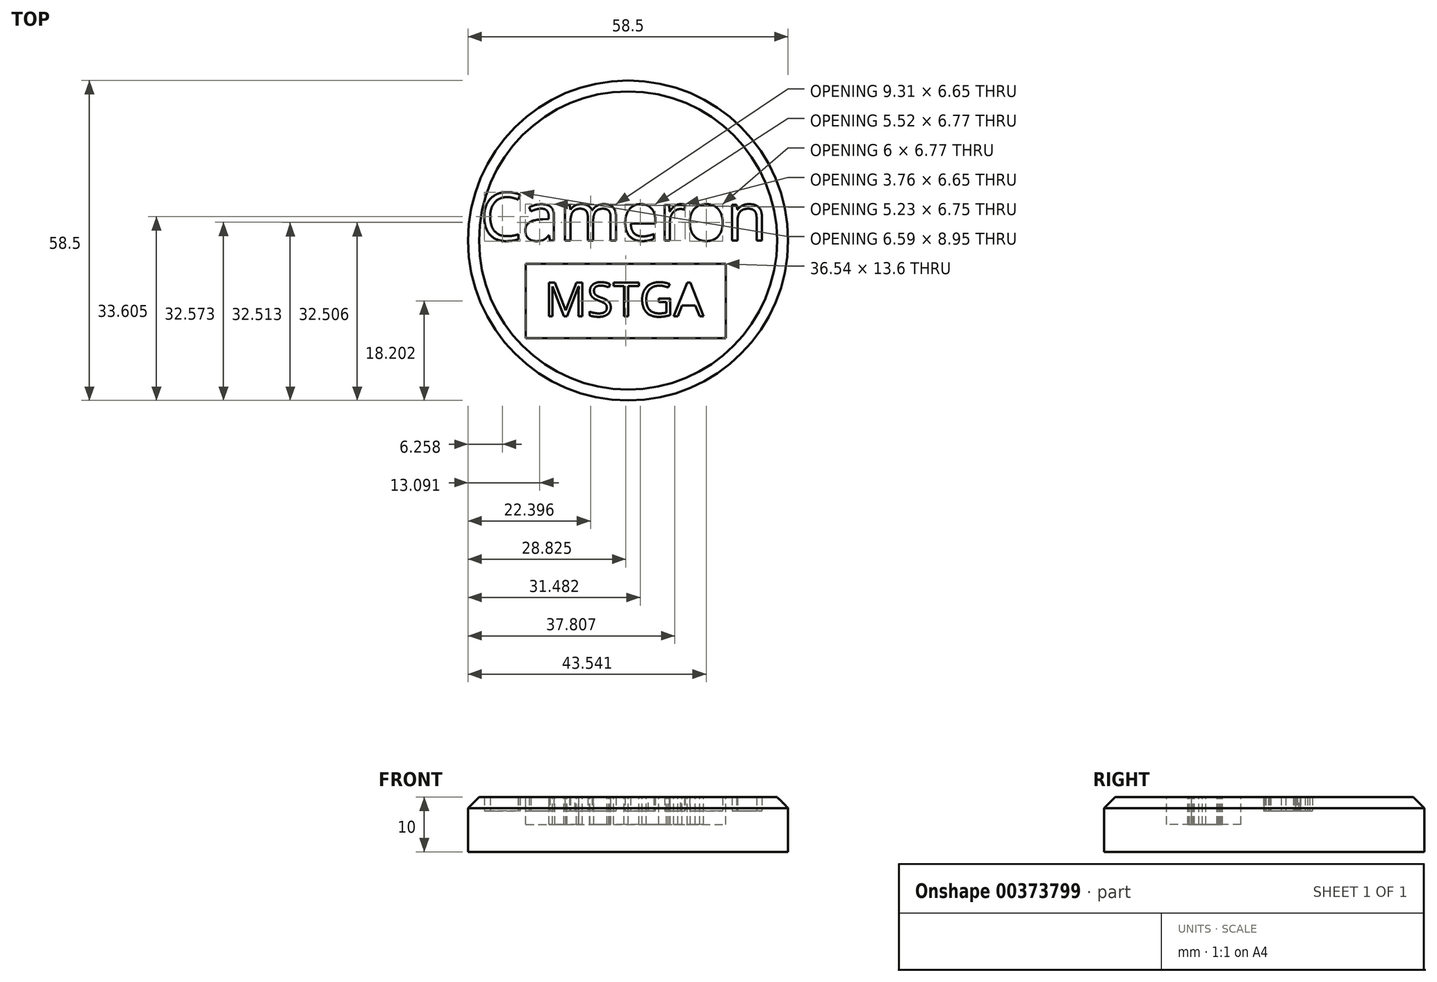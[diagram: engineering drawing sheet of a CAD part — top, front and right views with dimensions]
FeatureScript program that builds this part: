
annotation { "Feature Type Name" : "Feature", "Feature Type Description" : "" }
export const myFeature = defineFeature(function(context is Context, id is Id, definition is map)
    precondition{}
    {
        {
            var Q0;
            Q0=qCreatedBy(makeId("Top.planeOp"),FACE);
            var sketch = newSketch(context, id + "F0", { "sketchPlane" : qUnion([Q0])});
            skCircle(sketch, "E0", {"center": v(0, 0) * mm, "radius": 29.25 * mm});
            skSolve(sketch);
        }
        {
            var Q0;
            Q0=makeQuery(id+"F0.imprint","IMPRINT",FACE,{"disambiguationData":[TD([[makeQuery(id+"F0.imprint","IMPRINT",EDGE,{"derivedFrom":sQuery(id+"F0.wireOp",EDGE,"E0")}),1.0]])]});
            extrude(context, id + "F1", {"entities" : qUnion([Q0]), "depth" : 7.5 * mm});
        }
        {
            var Q0;
            Q0=makeQuery(id+"F1.opExtrude","CAP_FACE",FACE,{"disambiguationData":[OSD([sQuery(id+"F0.wireOp",EDGE,"E0")])],"isStart":false});
            var sketch = newSketch(context, id + "F2", { "sketchPlane" : qUnion([Q0])});
            skText(sketch, "E1", { "text": "Cameron", "fontName": "OpenSans-Regular.ttf"});
            const initialGuessF2  = {"E1": [-0.02703, 0, 1, 0, 0.00878]};
            skSetInitialGuess(sketch, initialGuessF2);
            skSolve(sketch);
        }
        {
            var Q0;
            Q0=makeQuery(id+"F2.imprint","IMPRINT",FACE,{"disambiguationData":[TD([[makeQuery(id+"F2.imprint","IMPRINT",EDGE,{"derivedFrom":sQuery(id+"F2.wireOp",EDGE,"E1.sketch_text.stroke-0")}),1.0]])]});
            extrude(context, id + "F3", {"entities" : qUnion([Q0]), "operationType" : NewBodyOperationType.ADD, "depth" : 2.5 * mm});
        }
        {
            var Q0;
            Q0=makeQuery(id+"F3.opExtrude","CAP_FACE",FACE,{"disambiguationData":[OSD([sQuery(id+"F0.wireOp",EDGE,"E0"),sQuery(id+"F2.wireOp",EDGE,"E1.sketch_text.stroke-0"),sQuery(id+"F2.wireOp",EDGE,"E1.sketch_text.stroke-1"),sQuery(id+"F2.wireOp",EDGE,"E1.sketch_text.stroke-2"),sQuery(id+"F2.wireOp",EDGE,"E1.sketch_text.stroke-3"),sQuery(id+"F2.wireOp",EDGE,"E1.sketch_text.stroke-4"),sQuery(id+"F2.wireOp",EDGE,"E1.sketch_text.stroke-5"),sQuery(id+"F2.wireOp",EDGE,"E1.sketch_text.stroke-6"),sQuery(id+"F2.wireOp",EDGE,"E1.sketch_text.stroke-7"),sQuery(id+"F2.wireOp",EDGE,"E1.sketch_text.stroke-8"),sQuery(id+"F2.wireOp",EDGE,"E1.sketch_text.stroke-9"),sQuery(id+"F2.wireOp",EDGE,"E1.sketch_text.stroke-10"),sQuery(id+"F2.wireOp",EDGE,"E1.sketch_text.stroke-11"),sQuery(id+"F2.wireOp",EDGE,"E1.sketch_text.stroke-12"),sQuery(id+"F2.wireOp",EDGE,"E1.sketch_text.stroke-13"),sQuery(id+"F2.wireOp",EDGE,"E1.sketch_text.stroke-14"),sQuery(id+"F2.wireOp",EDGE,"E1.sketch_text.stroke-15"),sQuery(id+"F2.wireOp",EDGE,"E1.sketch_text.stroke-16"),sQuery(id+"F2.wireOp",EDGE,"E1.sketch_text.stroke-17"),sQuery(id+"F2.wireOp",EDGE,"E1.sketch_text.stroke-18"),sQuery(id+"F2.wireOp",EDGE,"E1.sketch_text.stroke-19"),sQuery(id+"F2.wireOp",EDGE,"E1.sketch_text.stroke-20"),sQuery(id+"F2.wireOp",EDGE,"E1.sketch_text.stroke-21"),sQuery(id+"F2.wireOp",EDGE,"E1.sketch_text.stroke-22"),sQuery(id+"F2.wireOp",EDGE,"E1.sketch_text.stroke-23"),sQuery(id+"F2.wireOp",EDGE,"E1.sketch_text.stroke-24"),sQuery(id+"F2.wireOp",EDGE,"E1.sketch_text.stroke-25"),sQuery(id+"F2.wireOp",EDGE,"E1.sketch_text.stroke-26"),sQuery(id+"F2.wireOp",EDGE,"E1.sketch_text.stroke-27"),sQuery(id+"F2.wireOp",EDGE,"E1.sketch_text.stroke-28"),sQuery(id+"F2.wireOp",EDGE,"E1.sketch_text.stroke-29"),sQuery(id+"F2.wireOp",EDGE,"E1.sketch_text.stroke-30"),sQuery(id+"F2.wireOp",EDGE,"E1.sketch_text.stroke-31"),sQuery(id+"F2.wireOp",EDGE,"E1.sketch_text.stroke-32"),sQuery(id+"F2.wireOp",EDGE,"E1.sketch_text.stroke-33"),sQuery(id+"F2.wireOp",EDGE,"E1.sketch_text.stroke-42"),sQuery(id+"F2.wireOp",EDGE,"E1.sketch_text.stroke-43"),sQuery(id+"F2.wireOp",EDGE,"E1.sketch_text.stroke-44"),sQuery(id+"F2.wireOp",EDGE,"E1.sketch_text.stroke-45"),sQuery(id+"F2.wireOp",EDGE,"E1.sketch_text.stroke-46"),sQuery(id+"F2.wireOp",EDGE,"E1.sketch_text.stroke-47"),sQuery(id+"F2.wireOp",EDGE,"E1.sketch_text.stroke-48"),sQuery(id+"F2.wireOp",EDGE,"E1.sketch_text.stroke-49"),sQuery(id+"F2.wireOp",EDGE,"E1.sketch_text.stroke-50"),sQuery(id+"F2.wireOp",EDGE,"E1.sketch_text.stroke-51"),sQuery(id+"F2.wireOp",EDGE,"E1.sketch_text.stroke-52"),sQuery(id+"F2.wireOp",EDGE,"E1.sketch_text.stroke-53"),sQuery(id+"F2.wireOp",EDGE,"E1.sketch_text.stroke-54"),sQuery(id+"F2.wireOp",EDGE,"E1.sketch_text.stroke-55"),sQuery(id+"F2.wireOp",EDGE,"E1.sketch_text.stroke-56"),sQuery(id+"F2.wireOp",EDGE,"E1.sketch_text.stroke-57"),sQuery(id+"F2.wireOp",EDGE,"E1.sketch_text.stroke-58"),sQuery(id+"F2.wireOp",EDGE,"E1.sketch_text.stroke-59"),sQuery(id+"F2.wireOp",EDGE,"E1.sketch_text.stroke-60"),sQuery(id+"F2.wireOp",EDGE,"E1.sketch_text.stroke-61"),sQuery(id+"F2.wireOp",EDGE,"E1.sketch_text.stroke-62"),sQuery(id+"F2.wireOp",EDGE,"E1.sketch_text.stroke-63"),sQuery(id+"F2.wireOp",EDGE,"E1.sketch_text.stroke-64"),sQuery(id+"F2.wireOp",EDGE,"E1.sketch_text.stroke-65"),sQuery(id+"F2.wireOp",EDGE,"E1.sketch_text.stroke-66"),sQuery(id+"F2.wireOp",EDGE,"E1.sketch_text.stroke-67"),sQuery(id+"F2.wireOp",EDGE,"E1.sketch_text.stroke-68"),sQuery(id+"F2.wireOp",EDGE,"E1.sketch_text.stroke-69"),sQuery(id+"F2.wireOp",EDGE,"E1.sketch_text.stroke-70"),sQuery(id+"F2.wireOp",EDGE,"E1.sketch_text.stroke-71"),sQuery(id+"F2.wireOp",EDGE,"E1.sketch_text.stroke-72"),sQuery(id+"F2.wireOp",EDGE,"E1.sketch_text.stroke-73"),sQuery(id+"F2.wireOp",EDGE,"E1.sketch_text.stroke-74"),sQuery(id+"F2.wireOp",EDGE,"E1.sketch_text.stroke-75"),sQuery(id+"F2.wireOp",EDGE,"E1.sketch_text.stroke-76"),sQuery(id+"F2.wireOp",EDGE,"E1.sketch_text.stroke-77"),sQuery(id+"F2.wireOp",EDGE,"E1.sketch_text.stroke-78"),sQuery(id+"F2.wireOp",EDGE,"E1.sketch_text.stroke-79"),sQuery(id+"F2.wireOp",EDGE,"E1.sketch_text.stroke-80"),sQuery(id+"F2.wireOp",EDGE,"E1.sketch_text.stroke-81"),sQuery(id+"F2.wireOp",EDGE,"E1.sketch_text.stroke-82"),sQuery(id+"F2.wireOp",EDGE,"E1.sketch_text.stroke-83"),sQuery(id+"F2.wireOp",EDGE,"E1.sketch_text.stroke-89"),sQuery(id+"F2.wireOp",EDGE,"E1.sketch_text.stroke-90"),sQuery(id+"F2.wireOp",EDGE,"E1.sketch_text.stroke-91"),sQuery(id+"F2.wireOp",EDGE,"E1.sketch_text.stroke-92"),sQuery(id+"F2.wireOp",EDGE,"E1.sketch_text.stroke-93"),sQuery(id+"F2.wireOp",EDGE,"E1.sketch_text.stroke-94"),sQuery(id+"F2.wireOp",EDGE,"E1.sketch_text.stroke-95"),sQuery(id+"F2.wireOp",EDGE,"E1.sketch_text.stroke-96"),sQuery(id+"F2.wireOp",EDGE,"E1.sketch_text.stroke-97"),sQuery(id+"F2.wireOp",EDGE,"E1.sketch_text.stroke-98"),sQuery(id+"F2.wireOp",EDGE,"E1.sketch_text.stroke-99"),sQuery(id+"F2.wireOp",EDGE,"E1.sketch_text.stroke-100"),sQuery(id+"F2.wireOp",EDGE,"E1.sketch_text.stroke-101"),sQuery(id+"F2.wireOp",EDGE,"E1.sketch_text.stroke-102"),sQuery(id+"F2.wireOp",EDGE,"E1.sketch_text.stroke-103"),sQuery(id+"F2.wireOp",EDGE,"E1.sketch_text.stroke-104"),sQuery(id+"F2.wireOp",EDGE,"E1.sketch_text.stroke-105"),sQuery(id+"F2.wireOp",EDGE,"E1.sketch_text.stroke-106"),sQuery(id+"F2.wireOp",EDGE,"E1.sketch_text.stroke-107"),sQuery(id+"F2.wireOp",EDGE,"E1.sketch_text.stroke-108"),sQuery(id+"F2.wireOp",EDGE,"E1.sketch_text.stroke-109"),sQuery(id+"F2.wireOp",EDGE,"E1.sketch_text.stroke-110"),sQuery(id+"F2.wireOp",EDGE,"E1.sketch_text.stroke-119"),sQuery(id+"F2.wireOp",EDGE,"E1.sketch_text.stroke-120"),sQuery(id+"F2.wireOp",EDGE,"E1.sketch_text.stroke-121"),sQuery(id+"F2.wireOp",EDGE,"E1.sketch_text.stroke-122"),sQuery(id+"F2.wireOp",EDGE,"E1.sketch_text.stroke-123"),sQuery(id+"F2.wireOp",EDGE,"E1.sketch_text.stroke-124"),sQuery(id+"F2.wireOp",EDGE,"E1.sketch_text.stroke-125"),sQuery(id+"F2.wireOp",EDGE,"E1.sketch_text.stroke-126"),sQuery(id+"F2.wireOp",EDGE,"E1.sketch_text.stroke-127"),sQuery(id+"F2.wireOp",EDGE,"E1.sketch_text.stroke-128"),sQuery(id+"F2.wireOp",EDGE,"E1.sketch_text.stroke-129"),sQuery(id+"F2.wireOp",EDGE,"E1.sketch_text.stroke-130"),sQuery(id+"F2.wireOp",EDGE,"E1.sketch_text.stroke-131"),sQuery(id+"F2.wireOp",EDGE,"E1.sketch_text.stroke-132"),sQuery(id+"F2.wireOp",EDGE,"E1.sketch_text.stroke-133"),sQuery(id+"F2.wireOp",EDGE,"E1.sketch_text.stroke-134"),sQuery(id+"F2.wireOp",EDGE,"E1.sketch_text.stroke-135")])],"isStart":false});
            var sketch = newSketch(context, id + "F4", { "sketchPlane" : qUnion([Q0])});
            skLineSegment(sketch, "E2.bottom", {"start": v(-18.7, -4.25) * mm, "end": v(17.85, -4.25) * mm});
            skLineSegment(sketch, "E2.top", {"start": v(-18.7, -17.85) * mm, "end": v(17.85, -17.85) * mm});
            skLineSegment(sketch, "E2.left", {"start": v(-18.7, -4.25) * mm, "end": v(-18.7, -17.85) * mm});
            skLineSegment(sketch, "E2.right", {"start": v(17.85, -4.25) * mm, "end": v(17.85, -17.85) * mm});
            skText(sketch, "E3", { "text": "MSTGA\n", "fontName": "OpenSans-Regular.ttf"});
            const initialGuessF4  = {"E3": [-0.0153, -0.01388, 1, 0, 0.00623]};
            skSetInitialGuess(sketch, initialGuessF4);
            skSolve(sketch);
        }
        {
            var Q0;
            Q0=makeQuery(id+"F4.imprint","IMPRINT",FACE,{"disambiguationData":[TD([[makeQuery(id+"F4.imprint","IMPRINT",EDGE,{"derivedFrom":sQuery(id+"F4.wireOp",EDGE,"E2.bottom")}),-1.0]])]});
            extrude(context, id + "F5", {"entities" : qUnion([Q0]), "operationType" : NewBodyOperationType.REMOVE, "oppositeDirection" : true, "depth" : 5 * mm});
        }
        {
            var Q0;
            Q0=makeQuery(id+"F3.opExtrude","CAP_EDGE",EDGE,{"disambiguationData":[OSD([sQuery(id+"F0.wireOp",EDGE,"E0")])],"isStart":false});
            chamfer(context, id + "F6", {"entities" : qUnion([Q0]), "width" : 2 * mm, "tangentPropagation" : true});
        }
        {
            var Q0;
            Q0=makeQuery(id+"F1.opExtrude","SWEPT_BODY",BODY,{"disambiguationData":[OSD([sQuery(id+"F0.wireOp",EDGE,"E0")])]});
            transform(context, id + "F7", {"entities" : qUnion([Q0]), "transformType" : TransformType.TRANSLATION_3D, "dx" : 0 * mm, "dy" : 0 * mm, "dz" : 0 * mm, "makeCopy" : true});
        }
    });
